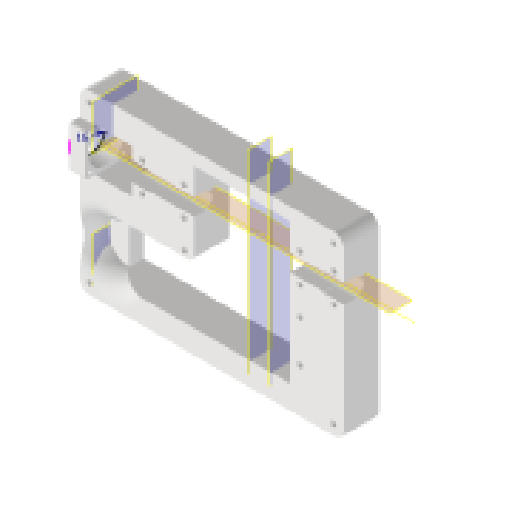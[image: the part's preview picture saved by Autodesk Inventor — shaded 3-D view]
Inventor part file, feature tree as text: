
AUTODESK INVENTOR PART (.ipt)
format: ipt  version: 2025.3 (Build 293356000, 356)  size: 593,408 bytes
history: native  units: mm
features: reference x17, extrude x16, other x14, sketch x13, projected_geometry x12, plane x6, fillet x3, hole x3, chamfer x1
ambient origin geometry x8: Origin, YZ Plane, XZ Plane, XY Plane, X Axis, Y Axis, Z Axis, Center Point
bodies: Solid1 (feature_tree)
feature tree (85):
  extrude  "Extrusion1"  Depth=12.0mm
  fillet  "Fillet1"  Radius=12.0mm
  plane  "Work Plane1"
  plane  "Work Plane2"
  plane  "Work Plane3"
  plane  "Work Plane4"
  plane  "Work Plane5"
  plane  "Arbeitsebene7"
  extrude  "Extrusion27"  [1 undecoded]
  extrude  "Extrusion28"  Depth=20.0mm TaperAngle=0.0deg
  extrude  "Extrusion29"  Depth=0.5mm
  extrude  "Extrusion37"  Depth=10.0mm
  extrude  "Extrusion38"  Depth=14.0mm
  fillet  "Rundung7"  Radius=10.0mm
  extrude  "Extrusion39"  TaperAngle=0.0deg  [1 undecoded]
  other  "Arbeitsachse1"
  extrude  "Extrusion42"  Depth=14.0mm
  hole  "Bohrung3"  [1 undecoded]
  hole  "Bohrung4"  [1 undecoded]
  extrude  "Extrusion47"  Depth=2.8mm
  fillet  "Rundung9"  Radius=2.8mm
  extrude  "Extrusion49"  TaperAngle=0.0deg  [1 undecoded]
  extrude  "Extrusion50"  Depth=5.0mm
  extrude  "Extrusion51"  Depth=20.0mm
  extrude  "Extrusion52"  Depth=10.0mm TaperAngle=0.0deg
  extrude  "Extrusion53"  Depth=10.0mm
  chamfer  "Fasen4"  Distance=25.0mm
  hole  "Bohrung5"  [1 undecoded]
  extrude  "Extrusion55"  Depth=5.0mm
  extrude  "Extrusion56"  Depth=5.0mm
  reference  "Referenz13"
  reference  "Referenz14"
  sketch  "Skizze40"  dims[d0=127.8mm d1=85.5mm d2=12.0mm d3=0.0mm]
  projected_geometry  "Projizierte Kontur18"
  sketch  "Skizze41"  dims[d4=4.0mm d38=-10.0mm]
  projected_geometry  "Projizierte Kontur19"
  sketch  "Skizze42"  dims[d142=0.5mm d143=20.0mm d144=0.0mm]
  reference  "Referenz22"
  reference  "Referenz23"
  reference  "Referenz24"
  reference  "Referenz25"
  sketch  "Skizze46"  dims[d145=8.0mm d146=0.0mm d147=0.5mm]
  projected_geometry  "Projizierte Kontur20"
  reference  "Referenz30"
  reference  "Referenz31"
  reference  "Referenz32"
  sketch  "Skizze54"  dims[d148=1.0mm d149=0.0mm d178=10.0mm]
  reference  "Referenz33"
  reference  "Referenz34"
  reference  "Referenz35"
  reference  "Referenz36"
  reference  "Referenz37"
  sketch  "Skizze57"  dims[d179=0.0mm d180=0.0mm d181=14.0mm d182=10.0mm d183=0.0mm]
  reference  "Referenz38"
  sketch  "Skizze58"  dims[d184=5.0mm d187=0.0mm d188=0.0mm]
  sketch  "Skizze59"  dims[d199=14.0mm d201=0.5mm]
  projected_geometry  "Projizierte Kontur27"
  projected_geometry  "Projizierte Kontur28"
  projected_geometry  "Projizierte Kontur29"
  sketch  "Skizze60"  dims[d203=0.5mm d204=1.0mm]
  projected_geometry  "Projizierte Kontur30"
  sketch  "Skizze61"  dims[d205=3.0mm d206=2.8mm]
  projected_geometry  "Projizierte Kontur31"
  projected_geometry  "Projizierte Kontur32"
  projected_geometry  "Projizierte Kontur33"
  sketch  "Skizze63"  dims[d207=2.8mm d208=2.8mm d209=2.8mm]
  reference  "Referenz39"
  reference  "Referenz40"
  sketch  "Skizze64"  dims[d210=2.8mm d211=0.0mm d212=0.0mm]
  projected_geometry  "Projizierte Kontur35"
  sketch  "Skizze65"  dims[d233=2.8mm d234=6.0mm d235=6.5mm d236=3.0mm d237=90.0deg d238=8.0mm d239=20.594885mm d240=16.0mm d241=2.5mm d242=6.0mm d243=4.0mm d244=2.0mm d245=90.0deg d246=8.0mm d247=20.594885mm d248=20.0mm d249=10.0mm d250=0.0mm d251=10.0mm d254=25.0mm d255=1.0mm d256=1.0mm d257=15.0mm d258=8.2mm d259=10.0mm d260=0.0mm d261=2.8mm d262=2.8mm d263=7.0mm d264=7.0mm d265=2.8mm d266=2.8mm d267=2.8mm d268=2.8mm d269=20.0mm d270=20.0mm d271=5.0mm d272=5.0mm d273=9.2mm d274=10.0mm d275=0.0mm d276=9.2mm d277=10.0mm d278=0.0mm d279=5.0mm d280=0.0mm d281=8.0mm d282=0.0mm d283=2.0mm d284=2.0mm d285=45.0deg d288=2.5mm d289=6.0mm d290=6.5mm d291=5.0mm d292=90.0deg d293=8.0mm d294=150.0deg d295=8.0mm d296=0.0mm d297=8.0mm d298=0.0mm d299=0.0mm d300=0.872665mm]
  projected_geometry  "Projizierte Kontur36"
  other  "<userpath>\Documents\GitHub\Guinardia\INVENTOR\Assembly_Guinardia_V1.iam"
  other  "Assembly_Guinardia_V1.iam"
  other  "00_NEMA8:1"
  other  "Assembly_Guinardia_V2.iam"
  other  "Assemlby_Scanner_v1:1"
  other  "30_Scanlens_Laseradaper_v1:1"
  other  "30_Scanlens_Laseradaper_lid_v1:1"
  other  "Assembly_HoliSheet_v6.iam"
  other  "11_Wellplatespacer:1"
  other  "<userpath>\Documents\HoLiSheet\INVENTOR\Assembly_HoliSheet_v6.iam"
  other  "00_NEMA8:2"
  other  "<userpath>\Documents\Inventor\Guinardia\INVENTOR\Assembly_Guinardia_V0.iam"
  other  "Assembly_Guinardia_V0.iam"
note: 6 required parameter values undecoded (feature->parameter linkage not recoverable at this tier; creation-order binding heuristic only, values carry confidence <= 0.55)
